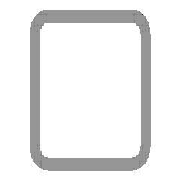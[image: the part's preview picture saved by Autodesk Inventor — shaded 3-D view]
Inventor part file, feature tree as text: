
AUTODESK INVENTOR PART (.ipt)
format: ipt  version: 2021 (Build 250183000, 183)  size: 140,288 bytes
history: native  units: mm (DEFAULTED — no unit token found)
features: other x5, sketch x3, extrude x1, split x1, plane x1
ambient origin geometry x8: Origin, YZ Plane, XZ Plane, XY Plane, X Axis, Y Axis, Z Axis, Center Point
bodies: Solid1 (feature_tree)
feature tree (11):
  parser-record x1  (decoder bookkeeping rows leaked as tree rows — omitted from the tree; the rows remain in map.json)
  other  "Driven Length"
  other  "Plano inicial"
  other  "Plano final"
  extrude  "Corpo"  TaperAngle=0.0deg  [1 undecoded]
  other  "Plano de trabalho4"
  split  "Dividir1"
  sketch  "Esboço"  dims[d11=50.8mm d12=4.7625mm d13=-0.0mm d14=2250.425546mm d15=25.4mm d16=25.4mm d17=9.525mm d18=90.0deg d19=2250.425546mm]
  sketch  "Sketch3"  dims[d3=2249.04731mm d4=0.0mm]
  plane  "Work Plane3"
  sketch  "Sketch4"  dims[d10=50.8mm]
note: 1 required parameter value undecoded (feature->parameter linkage not recoverable at this tier; creation-order binding heuristic only, values carry confidence <= 0.55)
